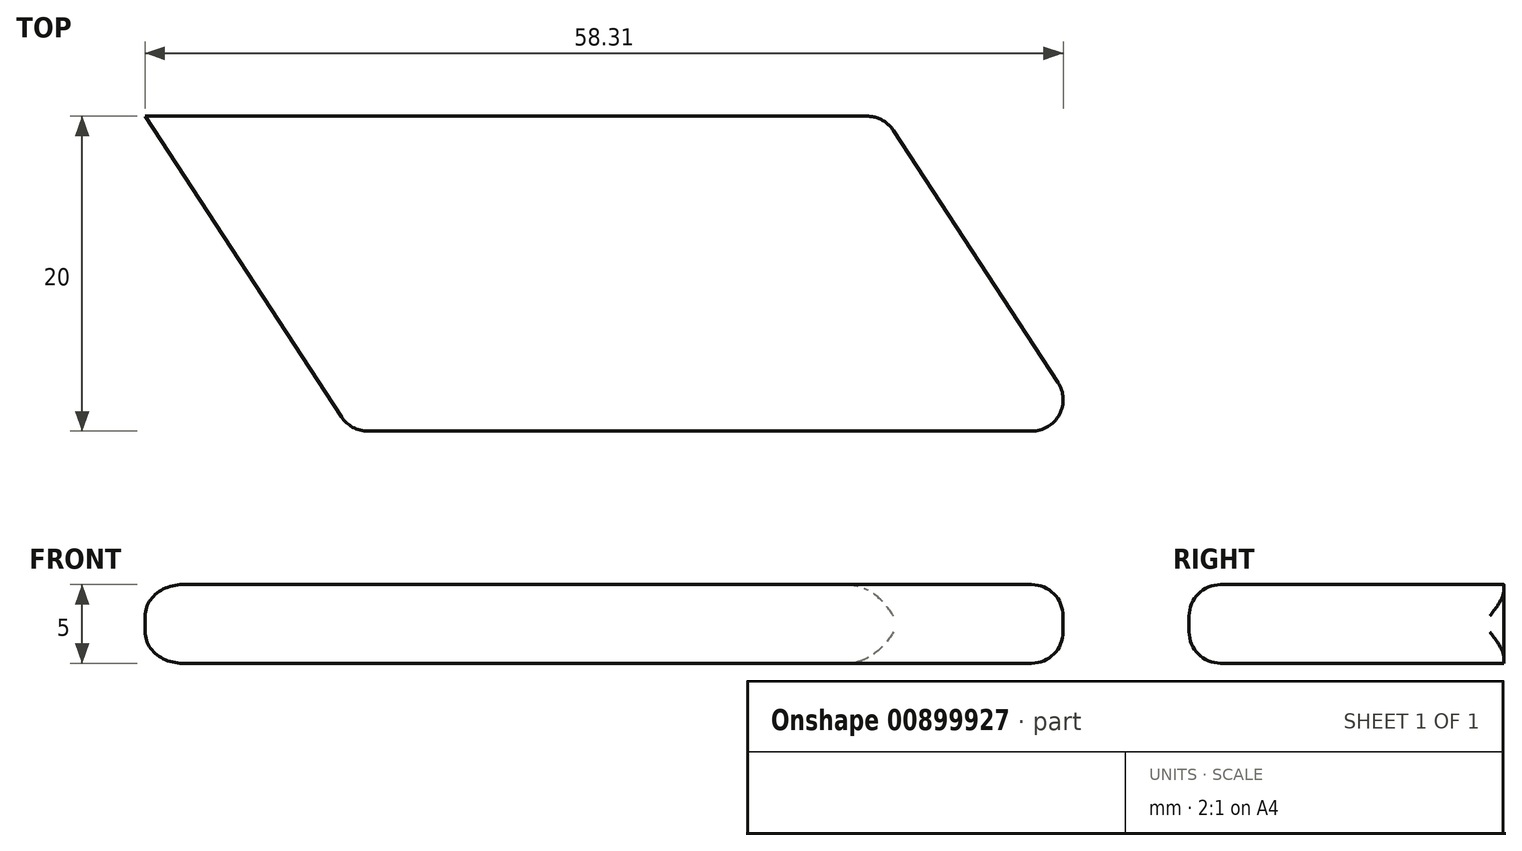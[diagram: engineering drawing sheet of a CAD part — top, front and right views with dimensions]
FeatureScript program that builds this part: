
annotation { "Feature Type Name" : "Feature", "Feature Type Description" : "" }
export const myFeature = defineFeature(function(context is Context, id is Id, definition is map)
    precondition{}
    {
        {
            var Q0;
            Q0=qCreatedBy(makeId("Top.planeOp"),FACE);
            var sketch = newSketch(context, id + "F0", { "sketchPlane" : qUnion([Q0])});
            skLineSegment(sketch, "E0.bottom", {"start": v(-30, 10) * mm, "end": v(16.94, 10) * mm});
            skLineSegment(sketch, "E0.top", {"start": v(-16.94, -10) * mm, "end": v(30, -10) * mm});
            skPoint(sketch, "E0.middle", {"position": v(0, 0) * mm});
            skLineSegment(sketch, "E1", {"start": v(-30, 10) * mm, "end": v(-16.94, -10) * mm});
            skLineSegment(sketch, "E2", {"start": v(30, -10) * mm, "end": v(16.94, 10) * mm});
            skPoint(sketch, "E0.right.start.orphan", {"position": v(30, 10) * mm});
            skPoint(sketch, "E3.orphan", {"position": v(-30, -10) * mm});
            skSolve(sketch);
        }
        {
            var Q0;
            Q0=makeQuery(id+"F0.imprint","IMPRINT",FACE,{"disambiguationData":[TD([[makeQuery(id+"F0.imprint","IMPRINT",EDGE,{"derivedFrom":sQuery(id+"F0.wireOp",EDGE,"E0.bottom")}),-1.0]])]});
            extrude(context, id + "F1", {"entities" : qUnion([Q0]), "depth" : 5 * mm, "offsetDistance" : 25.4 * mm});
        }
        {
            var Q0;
            Q0=makeQuery(id+"F1.opExtrude","CAP_EDGE",EDGE,{"disambiguationData":[OSD([sQuery(id+"F0.wireOp",EDGE,"E0.top")])],"isStart":false});
            var Q1;
            Q1=makeQuery(id+"F1.opExtrude","CAP_EDGE",EDGE,{"disambiguationData":[OSD([sQuery(id+"F0.wireOp",EDGE,"E1")])],"isStart":false});
            var Q2;
            Q2=makeQuery(id+"F1.opExtrude","CAP_EDGE",EDGE,{"disambiguationData":[OSD([sQuery(id+"F0.wireOp",EDGE,"E1")])],"isStart":true});
            var Q3;
            Q3=makeQuery(id+"F1.opExtrude","CAP_EDGE",EDGE,{"disambiguationData":[OSD([sQuery(id+"F0.wireOp",EDGE,"E2")])],"isStart":false});
            var Q4;
            Q4=makeQuery(id+"F1.opExtrude","SWEPT_FACE",FACE,{"disambiguationData":[OSD([sQuery(id+"F0.wireOp",EDGE,"E2")])]});
            var Q5;
            Q5=makeQuery(id+"F1.opExtrude","CAP_EDGE",EDGE,{"disambiguationData":[OSD([sQuery(id+"F0.wireOp",EDGE,"E0.top")])],"isStart":true});
            var Q6;
            Q6=makeQuery(id+"F1.opExtrude","SWEPT_EDGE",EDGE,{"disambiguationData":[OSD([sQuery(id+"F0.wireOp",EDGE,"E0.top"),sQuery(id+"F0.wireOp",EDGE,"E1")])]});
            var Q7;
            Q7=makeQuery(id+"F1.opExtrude","SWEPT_EDGE",EDGE,{"disambiguationData":[OSD([sQuery(id+"F0.wireOp",EDGE,"E0.bottom"),sQuery(id+"F0.wireOp",EDGE,"E2")])]});
            fillet(context, id + "F2", {"entities" : qUnion([Q0, Q1, Q2, Q3, Q4, Q5, Q6, Q7]), "radius" : 2 * mm, "tangentPropagation" : true, "allowEdgeOverflow" : false});
        }
    });
